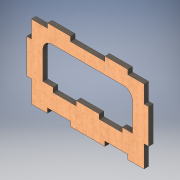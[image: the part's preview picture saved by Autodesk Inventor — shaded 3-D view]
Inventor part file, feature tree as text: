
AUTODESK INVENTOR PART (.ipt)
format: ipt  version: 2019 (Build 230136000, 136)  size: 241,664 bytes
history: native  units: mm
features: other x1, extrude x1, fillet x1
ambient origin geometry x8: Origin, YZ Plane, XZ Plane, XY Plane, X Axis, Y Axis, Z Axis, Center Point
bodies: Body1 (feature_tree)
feature tree (3):
  other  "Твердое тело1"
  extrude  "Выдавливание1"  Depth=30.0mm
  fillet  "Сопряжение1"  Radius=10.0mm
